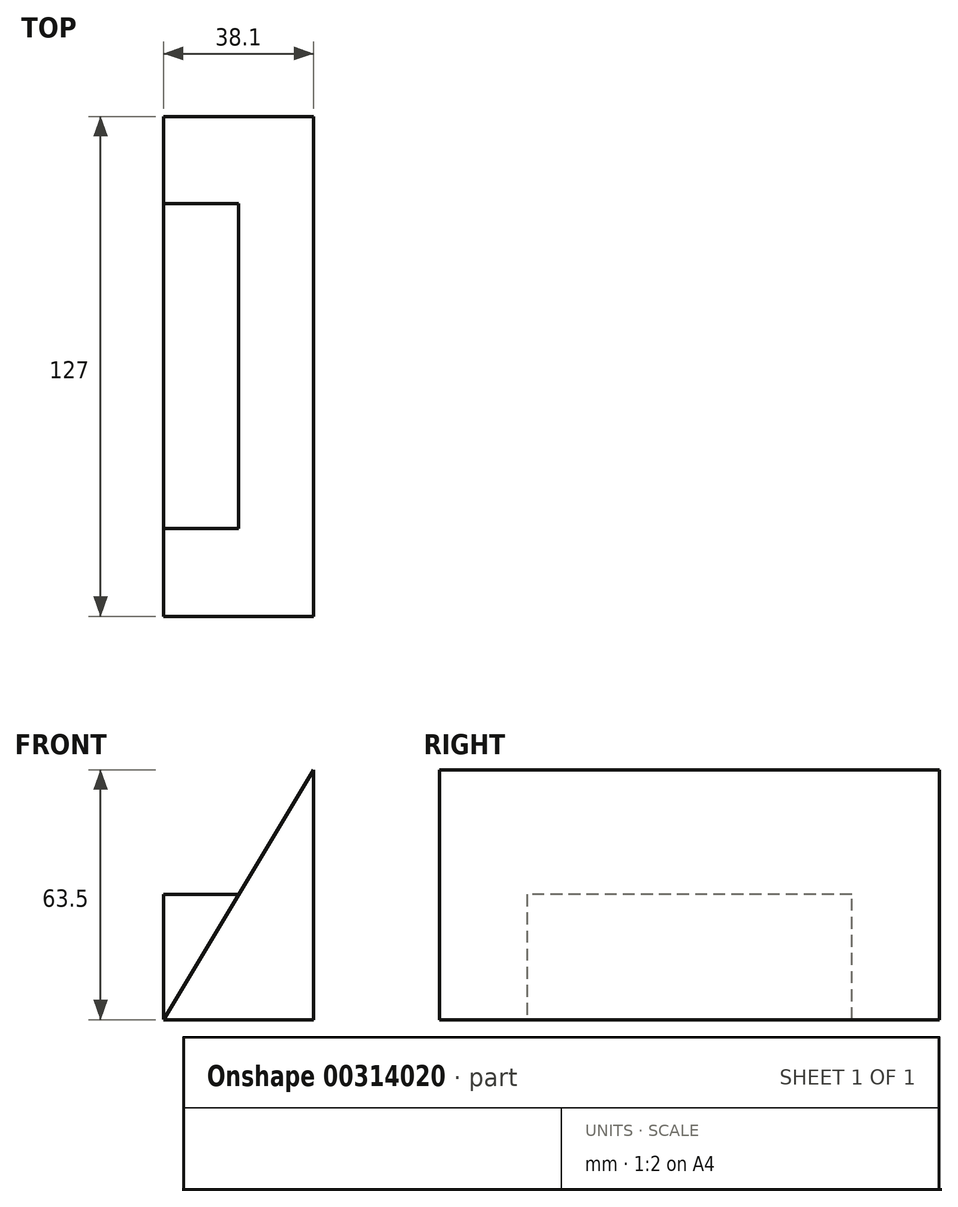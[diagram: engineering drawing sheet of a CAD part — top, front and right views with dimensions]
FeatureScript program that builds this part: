
annotation { "Feature Type Name" : "Feature", "Feature Type Description" : "" }
export const myFeature = defineFeature(function(context is Context, id is Id, definition is map)
    precondition{}
    {
        {
            var Q0;
            Q0=qCreatedBy(makeId("Front.planeOp"),FACE);
            var sketch = newSketch(context, id + "F0", { "sketchPlane" : qUnion([Q0])});
            skLineSegment(sketch, "E0", {"start": v(-26.48, -40.08) * mm, "end": v(11.62, -40.08) * mm});
            skLineSegment(sketch, "E1", {"start": v(11.62, -40.08) * mm, "end": v(11.62, 23.42) * mm});
            skLineSegment(sketch, "E2", {"start": v(11.62, 23.42) * mm, "end": v(-26.48, -40.08) * mm});
            skPoint(sketch, "E3.start.orphan", {"position": v(-7.43, -8.33) * mm});
            skSolve(sketch);
        }
        {
            var Q0;
            Q0=makeQuery(id+"F0.imprint","IMPRINT",FACE,{"disambiguationData":[TD([[makeQuery(id+"F0.imprint","IMPRINT",EDGE,{"derivedFrom":sQuery(id+"F0.wireOp",EDGE,"E0")}),1.0]])]});
            extrude(context, id + "F1", {"entities" : qUnion([Q0]), "depth" : 127 * mm});
        }
        {
            var Q0;
            Q0=qCreatedBy(makeId("Right.planeOp"),FACE);
            var sketch = newSketch(context, id + "F2", { "sketchPlane" : qUnion([Q0])});
            skLineSegment(sketch, "E4", {"start": v(-22.21, -40.03) * mm, "end": v(-22.21, -8.27) * mm});
            skLineSegment(sketch, "E5", {"start": v(-22.21, -8.27) * mm, "end": v(-104.76, -8.27) * mm});
            skLineSegment(sketch, "E6", {"start": v(-104.76, -8.27) * mm, "end": v(-104.76, -40.03) * mm});
            skLineSegment(sketch, "E7", {"start": v(-22.21, -40.03) * mm, "end": v(-104.76, -40.03) * mm});
            skSolve(sketch);
        }
        {
            var Q0;
            Q0 = qSketchRegion(id + "F2", true);
            extrude(context, id + "F3", {"entities" : qUnion([Q0]), "operationType" : NewBodyOperationType.ADD, "oppositeDirection" : true, "depth" : 26.42 * mm});
        }
    });
